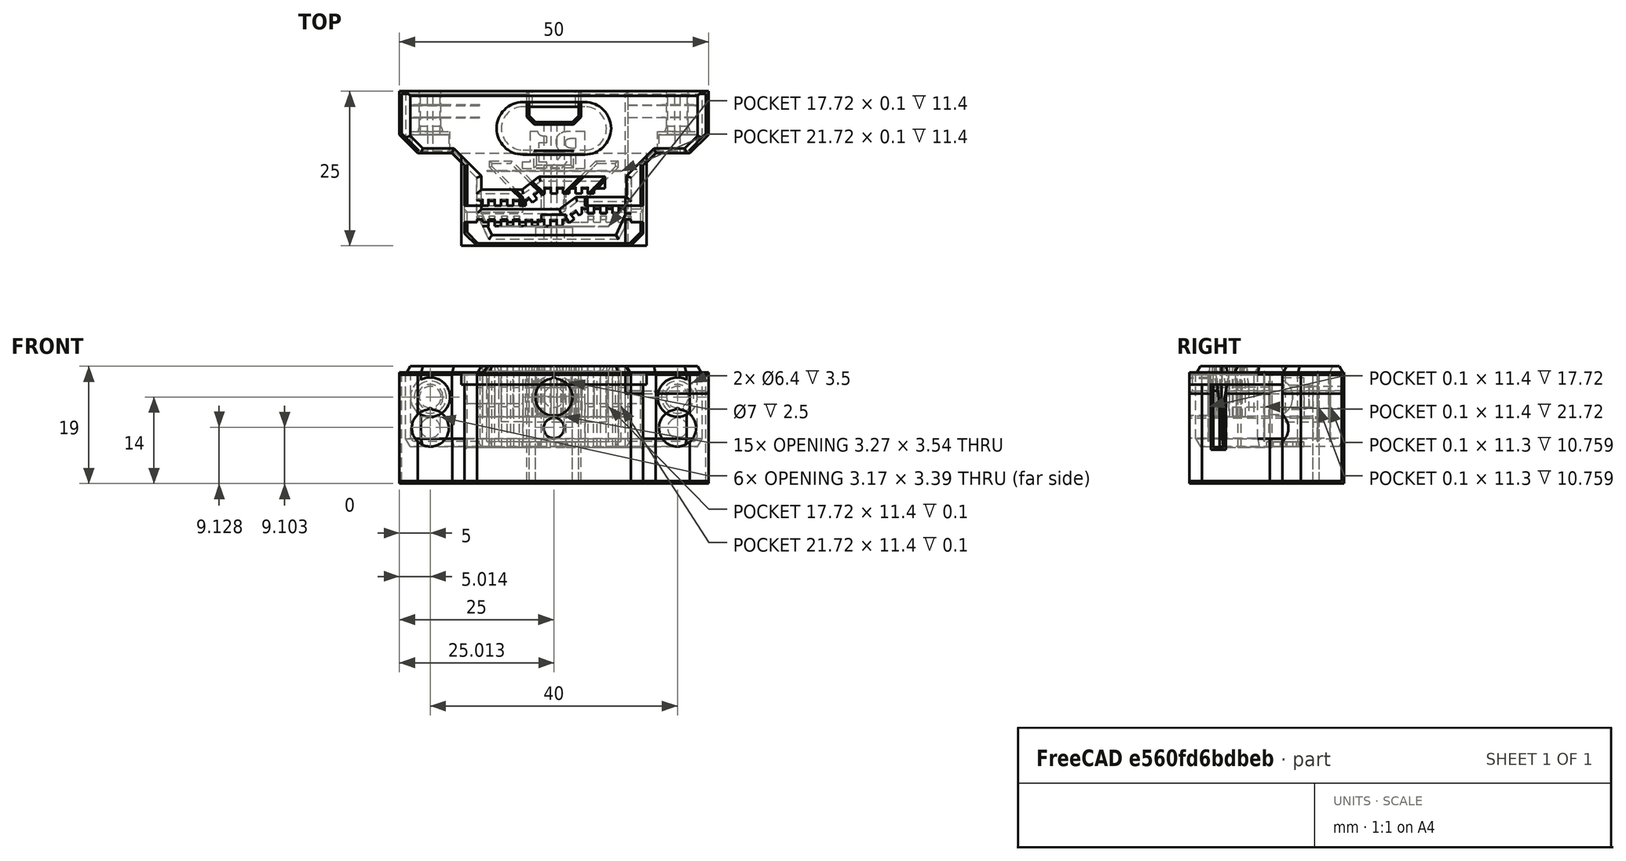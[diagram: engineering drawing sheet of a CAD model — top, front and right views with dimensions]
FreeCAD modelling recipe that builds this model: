
FCSTD DOCUMENT  (FreeCAD 0.18R16146 (Git))
Label: mini-bear-Y-belt-mounter
License: All rights reserved
LicenseURL: http://en.wikipedia.org/wiki/All_rights_reserved
objects: Part::Feature×19, Part::Box×16, Part::Cylinder×12, Part::Cut×12, Part::MultiFuse×11, Part::Chamfer×6
note: 76 computed .brp shape members not serialized (recipe doc carries the construction recipe); baked Part::Feature solids carry a one-line shape summary decoded from their .brp

FEATURE [Part::Box] Box  label="Cube"
  AttacherType = Attacher::AttachEngine3D
  Height = 12.1
  Length = 2
  Placement = pos=(0,0,-0.1) rot=(0,0,1;0rad)
  Width = 1
FEATURE [Part::Box] Box001  label="Cube001"
  AttacherType = Attacher::AttachEngine3D
  Height = 12.1
  Length = 0.9
  Placement = pos=(2,0,-0.1) rot=(0,0,1;0rad)
  Width = 2
FEATURE [Part::Box] Box002  label="Cube002"
  AttacherType = Attacher::AttachEngine3D
  Height = 12.1
  Length = 1.1
  Placement = pos=(2.9,0,-0.1) rot=(0,0,1;0rad)
  Width = 1
FEATURE [Part::Box] Box005  label="Cube005"
  AttacherType = Attacher::AttachEngine3D
  Height = 12.1
  Length = 30
  Placement = pos=(0,2.65,-0.1) rot=(0,0,1;0rad)
  Width = 6
FEATURE [Part::Chamfer] Chamfer
  Base = -> Box001
  Edges = 1 edges: [Edge12 r1=5.5 r2=0.57]
FEATURE [Part::MultiFuse] Fusion
  Shapes = -> [Chamfer,Box002]
FEATURE [Part::Feature] Fusion001 .. Fusion012  x12 (patterned run collapsed; names and placements below)
  shape: bbox 2 x 2 x 12.1 mm, 12 faces (baked)
  placements: 12 in arithmetic series — first pos=(2,0,0) rot=(0,0,1;0rad), step (2,0,0), last pos=(24,0,0) rot=(0,0,1;0rad)
FEATURE [Part::Box] Box006  label="Cube006"
  AttacherType = Attacher::AttachEngine3D
  Height = 12.1
  Length = 2
  Placement = pos=(26.9,0,-0.1) rot=(0,0,1;0rad)
  Width = 1
FEATURE [Part::MultiFuse] Fusion013
  Shapes = -> [Box,Fusion011,Fusion003,Fusion009,Fusion007,Box006,Fusion005,Fusion004,Fusion012,Fusion001,Fusion010,Fusion008,Fusion006,Fusion,Fusion002]
FEATURE [Part::Box] Box007  label="Cube007"
  AttacherType = Attacher::AttachEngine3D
  Height = 12.1
  Length = 28.9
  Placement = pos=(0,0,-0.1) rot=(0,0,1;0rad)
  Width = 8
FEATURE [Part::Box] Box008  label="Cube008"
  AttacherType = Attacher::AttachEngine3D
  Height = 18
  Length = 28.9
  Placement = pos=(-14.45,-25,-6) rot=(0,0,1;0rad)
  Width = 25
FEATURE [Part::Cylinder] Cylinder
  Angle = 360
  AttacherType = Attacher::AttachEngine3D
  Height = 10
  Placement = pos=(-20,-10,3) rot=(-1,0,0;1.5708rad)
  Radius = 1.6
FEATURE [Part::Cylinder] Cylinder001
  Angle = 360
  AttacherType = Attacher::AttachEngine3D
  Height = 10
  Placement = pos=(20,-10,3) rot=(-1,0,0;1.5708rad)
  Radius = 1.6
FEATURE [Part::Box] Box009  label="Cube009"
  AttacherType = Attacher::AttachEngine3D
  Height = 18
  Length = 50
  Placement = pos=(-25,-10,-6) rot=(0,0,1;0rad)
  Width = 10
FEATURE [Part::MultiFuse] Fusion014
  Shapes = -> [Fusion013,Box005]
FEATURE [Part::Chamfer] Chamfer001
  Base = -> Fusion014
  Edges = 1 edges: [Edge10 r1=5 r2=0.96]
FEATURE [Part::Cut] Cut  label="belt-teeth"
  Base = -> Box007
  Placement = pos=(-14.45,-22.15,0) rot=(0,0,1;0rad)
  Tool = -> Chamfer001
FEATURE [Part::MultiFuse] Fusion015
  Shapes = -> [Box009,Box008]
FEATURE [Part::Cylinder] Cylinder002
  Angle = 360
  AttacherType = Attacher::AttachEngine3D
  Height = 25
  Placement = pos=(0,1e-15,3) rot=(1,0,0;1.5708rad)
  Radius = 1.65
FEATURE [Part::Cylinder] Cylinder003
  Angle = 360
  AttacherType = Attacher::AttachEngine3D
  Height = 3
  Placement = pos=(0,-22,3) rot=(1,0,0;1.5708rad)
  Radius = 3
FEATURE [Part::Cylinder] Cylinder004
  Angle = 360
  AttacherType = Attacher::AttachEngine3D
  Height = 10
  Placement = pos=(-20,-10,3) rot=(-1,0,0;1.5708rad)
  Radius = 0.5
FEATURE [Part::Cylinder] Cylinder005
  Angle = 360
  AttacherType = Attacher::AttachEngine3D
  Height = 10
  Placement = pos=(20,-10,3) rot=(-1,0,0;1.5708rad)
  Radius = 0.5
FEATURE [Part::MultiFuse] Fusion016
  Placement = pos=(0,0,1.3) rot=(0,0,1;0rad)
  Shapes = -> [Cylinder005,Cylinder004]
FEATURE [Part::Cylinder] Cylinder006
  Angle = 360
  AttacherType = Attacher::AttachEngine3D
  Height = 3
  Placement = pos=(0,-22,5.7) rot=(1,0,0;1.5708rad)
  Radius = 0.5
FEATURE [Part::Cylinder] Cylinder007
  Angle = 360
  AttacherType = Attacher::AttachEngine3D
  Height = 25
  Placement = pos=(0,1e-15,4.4) rot=(1,0,0;1.5708rad)
  Radius = 0.5
FEATURE [Part::Box] Box010  label="Cube010"
  AttacherType = Attacher::AttachEngine3D
  Height = 12.1
  Length = 3
  Placement = pos=(-5,-21.15,-0.1) rot=(0,0,1;0rad)
  Width = 4
FEATURE [Part::Box] Box012  label="Cube012"
  AttacherType = Attacher::AttachEngine3D
  Height = 12.1
  Length = 3
  Placement = pos=(2,-21.15,-0.1) rot=(0,0,1;0rad)
  Width = 4
FEATURE [Part::Box] Box013  label="Cube013"
  AttacherType = Attacher::AttachEngine3D
  Height = 12.1
  Length = 10
  Placement = pos=(-5,-22,-0.1) rot=(0,0,1;0rad)
  Width = 10
FEATURE [Part::Cut] Cut001
  Base = -> Cut
  Tool = -> Box013
FEATURE [Part::MultiFuse] Fusion019
  Shapes = -> [Box012,Box010]
FEATURE [Part::Feature] Chamfer002001  label="Chamfer004"
  Placement = pos=(2,-17.15,0) rot=(0,0,1;0rad)
  shape: bbox 8 x 5.5 x 12.1 mm, 8 faces (baked)
FEATURE [Part::Feature] Chamfer003001  label="Chamfer006"
  Placement = pos=(-2,-17.15,0) rot=(0,0,1;0rad)
  shape: bbox 8 x 5.5 x 12.1 mm, 8 faces (baked)
FEATURE [Part::MultiFuse] Fusion020
  Shapes = -> [Chamfer003001,Chamfer002001]
FEATURE [Part::Box] Box016  label="Cube016"
  AttacherType = Attacher::AttachEngine3D
  Height = 12.1
  Length = 4
  Placement = pos=(-2,-20,-0.1) rot=(0,0,1;0rad)
  Width = 1
FEATURE [Part::Cut] Cut002
  Base = -> Fusion015
  Tool = -> Cut001
FEATURE [Part::Cut] Cut003
  Base = -> Cut002
  Tool = -> Fusion019
FEATURE [Part::Cut] Cut004
  Base = -> Cut003
  Tool = -> Fusion020
FEATURE [Part::Cut] Cut005
  Base = -> Cut004
  Tool = -> Box016
FEATURE [Part::Box] Box017  label="Cube017"
  AttacherType = Attacher::AttachEngine3D
  Height = 2
  Length = 30
  Placement = pos=(-15,-25,10) rot=(0,0,1;0rad)
  Width = 15
FEATURE [Part::Box] Box018  label="Cube018"
  AttacherType = Attacher::AttachEngine3D
  Height = 18
  Length = 8
  Placement = pos=(-4,2,-6) rot=(0,0,1;0rad)
  Width = 5
FEATURE [Part::Feature] Part__Feature009  label="MINI-y-belt-holder v1"
  Placement = pos=(0,-3.6e-14,-9e-15) rot=(0,0.707107,0.707107;3.14159rad)
  shape: bbox 48 x 24 x 132.5 mm, 275 faces (baked)
FEATURE [Part::Cylinder] Cylinder008
  Angle = 360
  AttacherType = Attacher::AttachEngine3D
  Height = 3
  Placement = pos=(-20,-8,3) rot=(1,0,0;1.5708rad)
  Radius = 0.5
FEATURE [Part::Cylinder] Cylinder009
  Angle = 360
  AttacherType = Attacher::AttachEngine3D
  Height = 3
  Placement = pos=(20,-8,3) rot=(1,0,0;1.5708rad)
  Radius = 0.5
FEATURE [Part::Cylinder] Cylinder010
  Angle = 360
  AttacherType = Attacher::AttachEngine3D
  Height = 3
  Placement = pos=(-20,-8,3) rot=(1,0,0;1.5708rad)
  Radius = 3
FEATURE [Part::Cylinder] Cylinder011
  Angle = 360
  AttacherType = Attacher::AttachEngine3D
  Height = 3
  Placement = pos=(20,-8,3) rot=(1,0,0;1.5708rad)
  Radius = 3
FEATURE [Part::MultiFuse] Fusion021
  Placement = pos=(0,0,2.7) rot=(0,0,1;0rad)
  Shapes = -> [Cylinder008,Cylinder009]
FEATURE [Part::Feature] Cylinder007001  label="Cylinder012"
  Placement = pos=(0,1e-15,4.4) rot=(1,0,0;1.5708rad)
  shape: bbox 1 x 25 x 1 mm, 3 faces (baked)
FEATURE [Part::Feature] Cylinder002001  label="Cylinder013"
  Placement = pos=(0,1e-15,3) rot=(1,0,0;1.5708rad)
  shape: bbox 3.3 x 25 x 3.3 mm, 3 faces (baked)
FEATURE [Part::MultiFuse] Fusion023
  Shapes = -> [Cylinder007,Cylinder002]
FEATURE [Part::MultiFuse] Fusion024
  Placement = pos=(0,0,5) rot=(0,0,1;0rad)
  Shapes = -> [Cylinder006,Cylinder003,Cylinder007001,Cylinder002001]
FEATURE [Part::Chamfer] Chamfer003002
  Base = -> Box018
  Edges = 2 edges r=1: [Edge1,Edge5]
  Placement = pos=(0,-7,0) rot=(0,0,1;0rad)
FEATURE [Part::Cut] Cut006
  Base = -> Cut005
  Tool = -> Chamfer003002
FEATURE [Part::Cut] Cut007
  Base = -> Cut006
  Tool = -> Fusion024
FEATURE [Part::Cut] Cut008
  Base = -> Cut007
  Tool = -> Fusion023
FEATURE [Part::Box] Box019  label="Cube019"
  AttacherType = Attacher::AttachEngine3D
  Height = 7.6
  Length = 5.6
  Placement = pos=(-2.8,-12,5.2) rot=(0,0,1;0rad)
  Width = 2
FEATURE [Part::MultiFuse] Fusion025
  Placement = pos=(0,1,0) rot=(0,0,1;0rad)
  Shapes = -> [Cylinder001,Fusion016,Cylinder,Cylinder010,Cylinder011,Fusion021]
FEATURE [Part::Chamfer] Chamfer003003
  Base = -> Cut008
  Edges = 2 edges r=3: [Edge1,Edge298]
FEATURE [Part::Chamfer] Chamfer003004
  Base = -> Chamfer003003
  Edges = 4 edges r=2: [Edge15,Edge42,Edge148,Edge170]
FEATURE [Part::Cut] Cut009
  Base = -> Chamfer003004
  Tool = -> Fusion025
FEATURE [Part::Cut] Cut010
  Base = -> Cut009
  Tool = -> Box019
FEATURE [Part::Feature] Cut010001  label="Cut011"
  shape: bbox 50 x 25 x 18 mm, 114 faces (baked)
FEATURE [Part::Box] Box020  label="Cube020"
  AttacherType = Attacher::AttachEngine3D
  Height = 10
  Length = 25
  Placement = pos=(12,-27,9) rot=(0,0,1;0rad)
  Width = 33
FEATURE [Part::Feature] Chamfer003005001  label="full-mounter001"
  shape: bbox 50 x 25 x 18 mm, 190 faces (baked)
FEATURE [Part::Cut] Cut010002
  Base = -> Cut010001
  Tool = -> Box020
FEATURE [Part::Chamfer] Chamfer003005002
  Base = -> Cut010002
  Edges = 66 edges r=0.4: [Edge2,Edge9,Edge10,Edge12,Edge13,Edge14,Edge15,Edge16,Edge17,Edge18,Edge19,Edge20,Edge21,Edge22,Edge24,Edge25,Edge26,Edge27,Edge28,Edge29,Edge31,Edge32,Edge33,Edge34,Edge35,Edge36,Edge38,Edge39,Edge40,Edge41,Edge42,Edge43,Edge51,Edge52,Edge53,Edge54,Edge55,Edge56,Edge57,Edge58,Edge59,Edge60,Edge61,+23 more]
